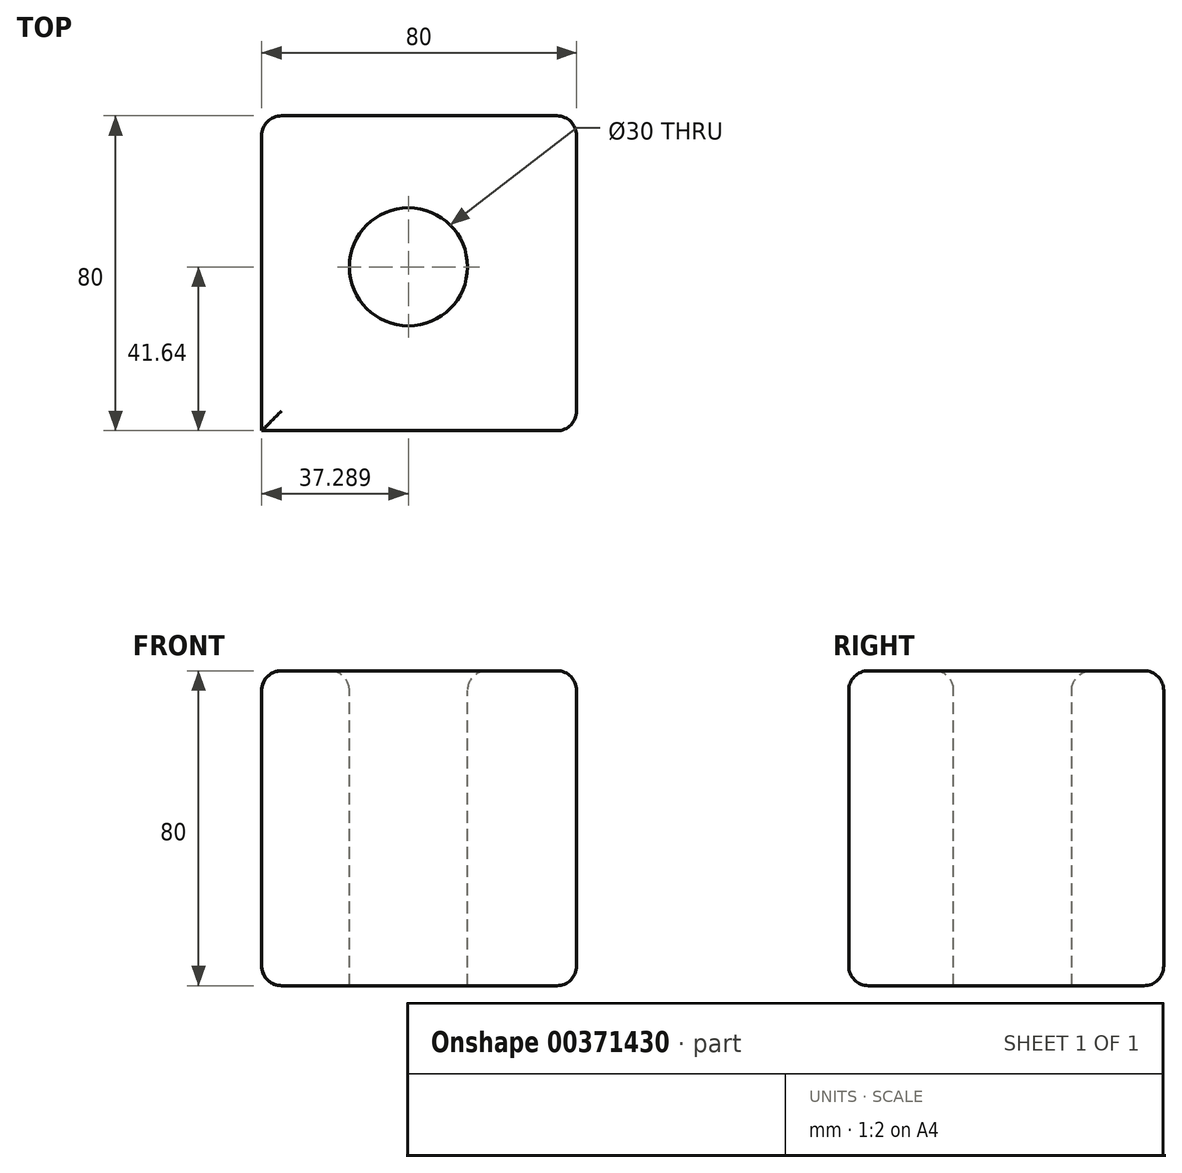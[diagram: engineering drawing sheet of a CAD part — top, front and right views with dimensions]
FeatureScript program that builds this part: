
annotation { "Feature Type Name" : "Feature", "Feature Type Description" : "" }
export const myFeature = defineFeature(function(context is Context, id is Id, definition is map)
    precondition{}
    {
        {
            var Q0;
            Q0=qCreatedBy(makeId("Top.planeOp"),FACE);
            var sketch = newSketch(context, id + "F0", { "sketchPlane" : qUnion([Q0])});
            skLineSegment(sketch, "E0.bottom", {"start": v(-19.43, 38.36) * mm, "end": v(60.57, 38.36) * mm});
            skLineSegment(sketch, "E0.top", {"start": v(-19.43, -41.64) * mm, "end": v(60.57, -41.64) * mm});
            skLineSegment(sketch, "E0.left", {"start": v(-19.43, 38.36) * mm, "end": v(-19.43, -41.64) * mm});
            skLineSegment(sketch, "E0.right", {"start": v(60.57, 38.36) * mm, "end": v(60.57, -41.64) * mm});
            skSolve(sketch);
        }
        {
            var Q0;
            Q0 = qSketchRegion(id + "F0", true);
            extrude(context, id + "F1", {"entities" : qUnion([Q0]), "depth" : 80 * mm});
        }
        {
            var Q0;
            Q0=makeQuery(id+"F1.opExtrude","CAP_FACE",FACE,{"disambiguationData":[OSD([sQuery(id+"F0.wireOp",EDGE,"E0.bottom"),sQuery(id+"F0.wireOp",EDGE,"E0.top"),sQuery(id+"F0.wireOp",EDGE,"E0.left"),sQuery(id+"F0.wireOp",EDGE,"E0.right")])],"isStart":false});
            var sketch = newSketch(context, id + "F2", { "sketchPlane" : qUnion([Q0])});
            skCircle(sketch, "E1", {"center": v(17.86, 0) * mm, "radius": 15 * mm});
            skSolve(sketch);
        }
        {
            var Q0;
            Q0=makeQuery(id+"F2.imprint","IMPRINT",FACE,{"disambiguationData":[TD([[makeQuery(id+"F2.imprint","IMPRINT",EDGE,{"derivedFrom":sQuery(id+"F2.wireOp",EDGE,"E1")}),1.0]])]});
            extrude(context, id + "F3", {"entities" : qUnion([Q0]), "operationType" : NewBodyOperationType.REMOVE, "endBound" : BoundingType.THROUGH_ALL, "oppositeDirection" : true, "depth" : 25 * mm});
        }
        {
            var Q0;
            Q0=makeQuery(id+"F1.opExtrude","CAP_EDGE",EDGE,{"disambiguationData":[OSD([sQuery(id+"F0.wireOp",EDGE,"E0.bottom")])],"isStart":true});
            var Q1;
            Q1=makeQuery(id+"F1.opExtrude","CAP_EDGE",EDGE,{"disambiguationData":[OSD([sQuery(id+"F0.wireOp",EDGE,"E0.right")])],"isStart":true});
            var Q2;
            Q2=makeQuery(id+"F1.opExtrude","CAP_EDGE",EDGE,{"disambiguationData":[OSD([sQuery(id+"F0.wireOp",EDGE,"E0.top")])],"isStart":true});
            var Q3;
            Q3=makeQuery(id+"F1.opExtrude","CAP_EDGE",EDGE,{"disambiguationData":[OSD([sQuery(id+"F0.wireOp",EDGE,"E0.left")])],"isStart":true});
            var Q4;
            Q4=makeQuery(id+"F1.opExtrude","CAP_EDGE",EDGE,{"disambiguationData":[OSD([sQuery(id+"F0.wireOp",EDGE,"E0.right")])],"isStart":false});
            var Q5;
            Q5=makeQuery(id+"F1.opExtrude","SWEPT_EDGE",EDGE,{"disambiguationData":[OSD([sQuery(id+"F0.wireOp",EDGE,"E0.top"),sQuery(id+"F0.wireOp",EDGE,"E0.right")])]});
            var Q6;
            Q6=makeQuery(id+"F1.opExtrude","SWEPT_FACE",FACE,{"disambiguationData":[OSD([sQuery(id+"F0.wireOp",EDGE,"E0.right")])]});
            var Q7;
            Q7=makeQuery(id+"F1.opExtrude","CAP_EDGE",EDGE,{"disambiguationData":[OSD([sQuery(id+"F0.wireOp",EDGE,"E0.bottom")])],"isStart":false});
            var Q8;
            Q8=makeQuery(id+"F1.opExtrude","CAP_FACE",FACE,{"disambiguationData":[OSD([sQuery(id+"F0.wireOp",EDGE,"E0.bottom"),sQuery(id+"F0.wireOp",EDGE,"E0.top"),sQuery(id+"F0.wireOp",EDGE,"E0.left"),sQuery(id+"F0.wireOp",EDGE,"E0.right")])],"isStart":false});
            var Q9;
            Q9=makeQuery(id+"F1.opExtrude","CAP_EDGE",EDGE,{"disambiguationData":[OSD([sQuery(id+"F0.wireOp",EDGE,"E0.left")])],"isStart":false});
            var Q10;
            Q10=makeQuery(id+"F1.opExtrude","SWEPT_EDGE",EDGE,{"disambiguationData":[OSD([sQuery(id+"F0.wireOp",EDGE,"E0.bottom"),sQuery(id+"F0.wireOp",EDGE,"E0.left")])]});
            fillet(context, id + "F4", {"entities" : qUnion([Q0, Q1, Q2, Q3, Q4, Q5, Q6, Q7, Q8, Q9, Q10]), "radius" : 5 * mm, "tangentPropagation" : true, "allowEdgeOverflow" : false});
        }
    });
